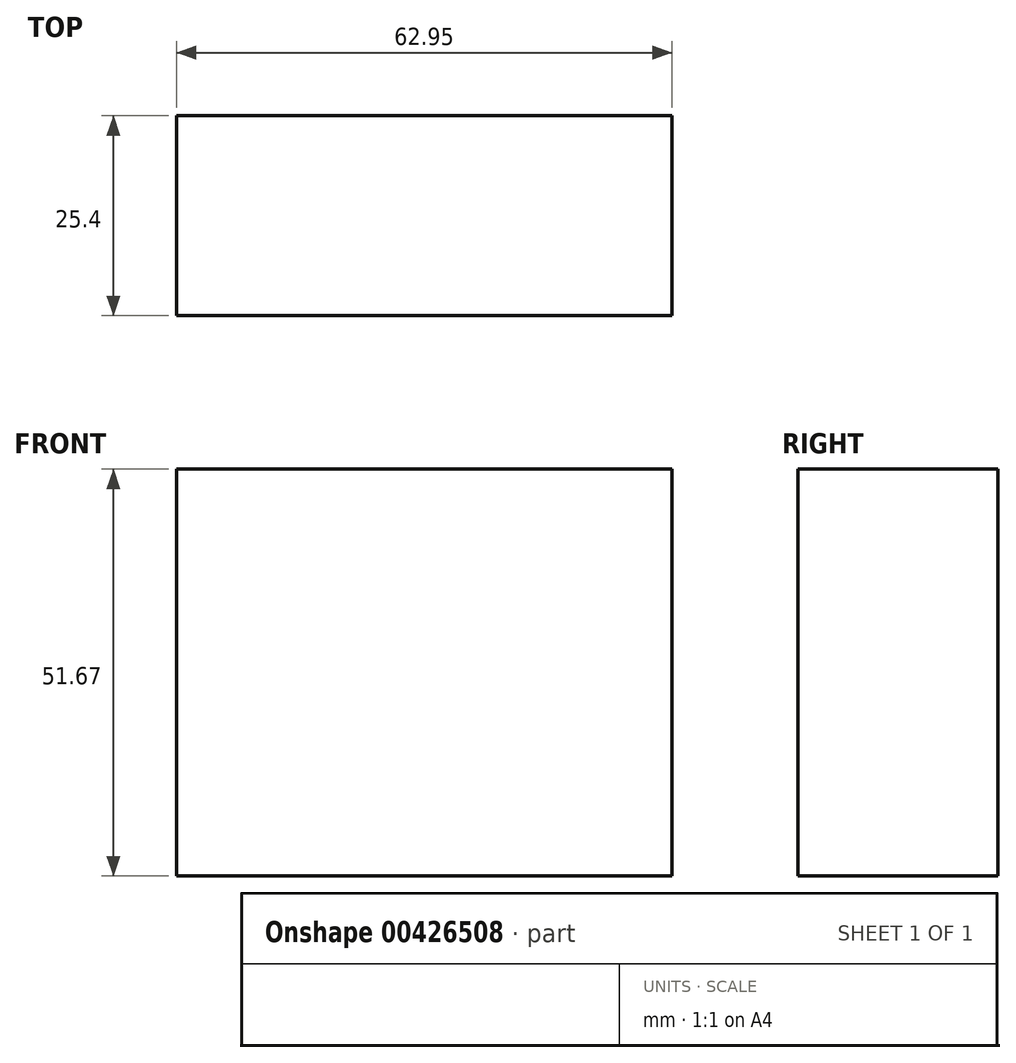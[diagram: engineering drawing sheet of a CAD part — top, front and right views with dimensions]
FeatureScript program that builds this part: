
annotation { "Feature Type Name" : "Feature", "Feature Type Description" : "" }
export const myFeature = defineFeature(function(context is Context, id is Id, definition is map)
    precondition{}
    {
        {
            var Q0;
            Q0=qCreatedBy(makeId("Front.planeOp"),FACE);
            var sketch = newSketch(context, id + "F0", { "sketchPlane" : qUnion([Q0])});
            skLineSegment(sketch, "E0.bottom", {"start": v(-13.26, 110.19) * mm, "end": v(49.69, 110.19) * mm});
            skLineSegment(sketch, "E0.top", {"start": v(-13.26, 58.52) * mm, "end": v(49.69, 58.52) * mm});
            skLineSegment(sketch, "E0.left", {"start": v(-13.26, 110.19) * mm, "end": v(-13.26, 58.52) * mm});
            skLineSegment(sketch, "E0.right", {"start": v(49.69, 110.19) * mm, "end": v(49.69, 58.52) * mm});
            skSolve(sketch);
        }
        {
            var Q0;
            Q0=makeQuery(id+"F0.imprint","IMPRINT",FACE,{"disambiguationData":[TD([[makeQuery(id+"F0.imprint","IMPRINT",EDGE,{"derivedFrom":sQuery(id+"F0.wireOp",EDGE,"E0.bottom")}),-1.0]])]});
            extrude(context, id + "F1", {"entities" : qUnion([Q0]), "depth" : 25.4 * mm});
        }
    });
